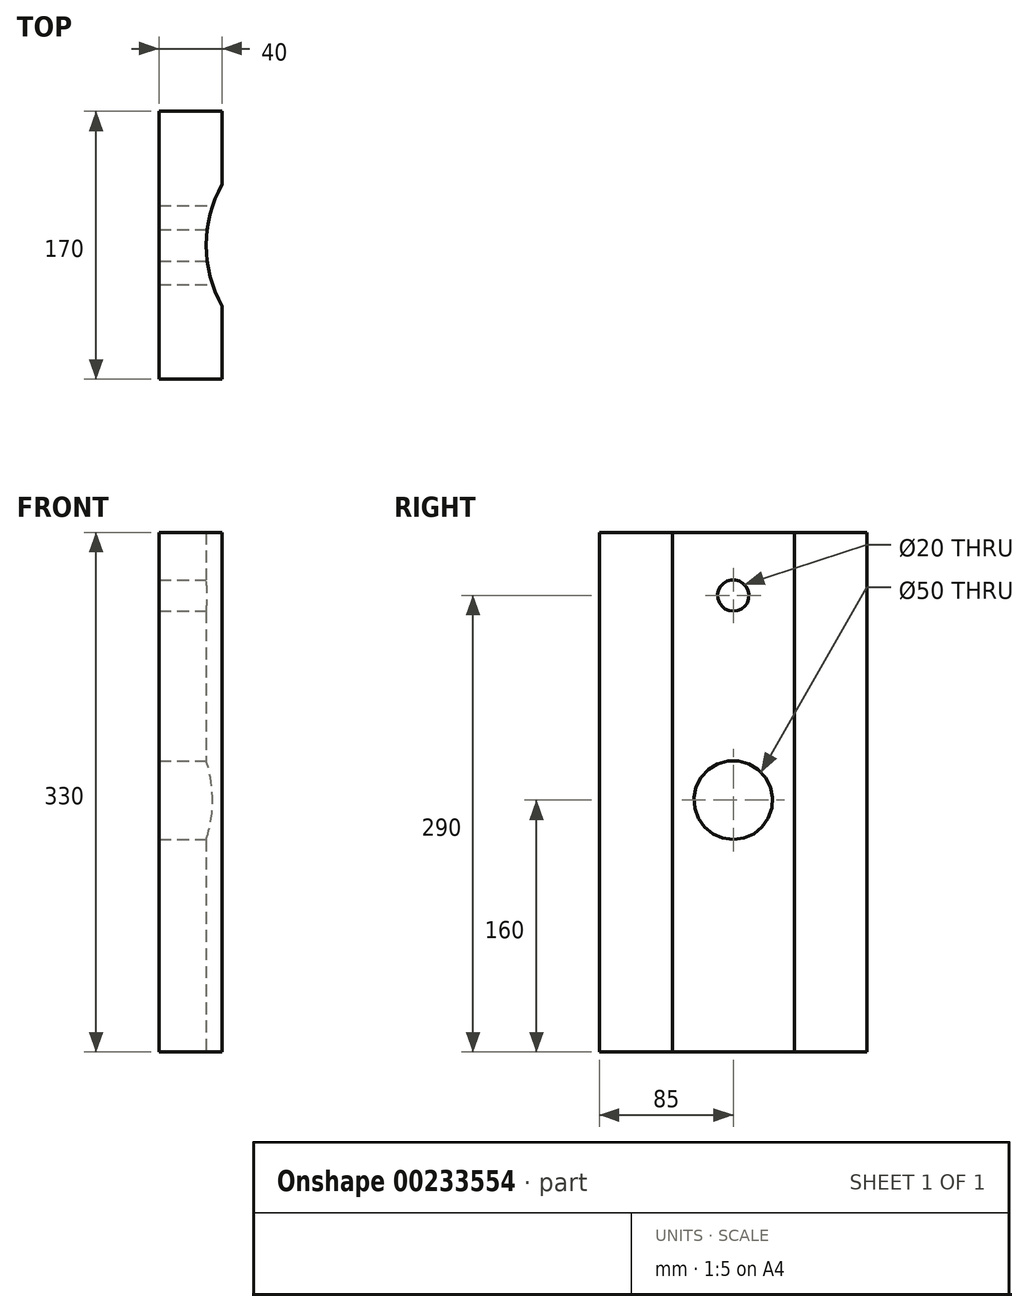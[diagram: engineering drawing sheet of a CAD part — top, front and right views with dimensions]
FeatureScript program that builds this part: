
annotation { "Feature Type Name" : "Feature", "Feature Type Description" : "" }
export const myFeature = defineFeature(function(context is Context, id is Id, definition is map)
    precondition{}
    {
        {
            var Q0;
            Q0=qCreatedBy(makeId("Right.planeOp"),FACE);
            var sketch = newSketch(context, id + "F0", { "sketchPlane" : qUnion([Q0])});
            skLineSegment(sketch, "E0.bottom", {"start": v(85, 165) * mm, "end": v(-85, 165) * mm});
            skLineSegment(sketch, "E0.top", {"start": v(85, -165) * mm, "end": v(-85, -165) * mm});
            skLineSegment(sketch, "E0.left", {"start": v(85, 165) * mm, "end": v(85, -165) * mm});
            skLineSegment(sketch, "E0.right", {"start": v(-85, 165) * mm, "end": v(-85, -165) * mm});
            skPoint(sketch, "E0.middle", {"position": v(0, 0) * mm});
            skCircle(sketch, "E1", {"center": v(0, -5) * mm, "radius": 25 * mm});
            skArc(sketch, "E2", {"start": v(-85, 93.36) * mm, "mid": v(0, 125) * mm, "end": v(85, 93.36) * mm, "construction": true});
            skCircle(sketch, "E3", {"center": v(0, 125) * mm, "radius": 10 * mm});
            skLineSegment(sketch, "E4", {"start": v(0, -5) * mm, "end": v(0, 165) * mm, "construction": true});
            skSolve(sketch);
        }
        {
            var Q0;
            Q0=makeQuery(id+"F0.imprint","IMPRINT",FACE,{"disambiguationData":[TD([[makeQuery(id+"F0.imprint","IMPRINT",EDGE,{"derivedFrom":sQuery(id+"F0.wireOp",EDGE,"E0.bottom")}),1.0]])]});
            var Q1;
            Q1=makeQuery(id+"F0.imprint","IMPRINT",FACE,{"disambiguationData":[TD([[makeQuery(id+"F0.imprint","IMPRINT",EDGE,{"derivedFrom":sQuery(id+"F0.wireOp",EDGE,"E1")}),1.0]])]});
            extrude(context, id + "F1", {"entities" : qUnion([Q0, Q1]), "oppositeDirection" : true, "depth" : 40 * mm});
        }
        {
            var Q0;
            Q0=sQuery(id+"F0.wireOp",VERTEX,"E1.center");
            var Q1;
            Q1=makeQuery(id+"F1.opExtrude","SWEPT_BODY",BODY,{"disambiguationData":[OSD([sQuery(id+"F0.wireOp",EDGE,"E0.bottom"),sQuery(id+"F0.wireOp",EDGE,"E0.top"),sQuery(id+"F0.wireOp",EDGE,"E0.left"),sQuery(id+"F0.wireOp",EDGE,"E0.right"),sQuery(id+"F0.wireOp",EDGE,"QbuMOewl-ePWH-L9PK-gwrw-fLn1AOVCfODG")])]});
            hole(context, id + "F2", {"style" : HoleStyle.SIMPLE, "endStyle" : HoleEndStyle.THROUGH, "holeDiameter" : 50 * mm, "startFromSketch" : true, "locations" : qUnion([Q0]), "scope" : qUnion([Q1]), "isTappedThrough" : true});
        }
        {
            var Q0;
            Q0=makeQuery(id+"F1.opExtrude","SWEPT_FACE",FACE,{"disambiguationData":[OSD([sQuery(id+"F0.wireOp",EDGE,"E0.top")])]});
            var sketch = newSketch(context, id + "F3", { "sketchPlane" : qUnion([Q0])});
            skArc(sketch, "E5", {"start": v(0, 38.73) * mm, "mid": v(-10, 0) * mm, "end": v(0, -38.73) * mm});
            skSolve(sketch);
        }
        {
            var Q0;
            {var subQ0=sQuery(id+"F3.wireOp",EDGE,"E5");Q0=makeQuery(id+"F3.imprint","IMPRINT",FACE,{"disambiguationData":[TD([[makeQuery(id+"F3.imprint","IMPRINT",EDGE,{"derivedFrom":subQ0}),1.0]])]});}
            extrude(context, id + "F4", {"entities" : qUnion([Q0]), "operationType" : NewBodyOperationType.REMOVE, "endBound" : BoundingType.THROUGH_ALL, "oppositeDirection" : true, "depth" : 25 * mm});
        }
    });
